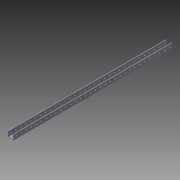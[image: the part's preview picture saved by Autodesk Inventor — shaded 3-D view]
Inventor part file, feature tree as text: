
AUTODESK INVENTOR PART (.ipt)
format: ipt  version: 2014 (Build 180170000, 170)  size: 183,296 bytes
history: native  units: in
note: dims shown in document units (in); Inventor stores cm internally (conversion verified against a paired STEP export)
features: sketch x3, hole x2, pattern_linear x2, extrude x1
ambient origin geometry x8: Origin, YZ Plane, XZ Plane, XY Plane, X Axis, Y Axis, Z Axis, Center Point
bodies: Solid1 (feature_tree)
feature tree (8):
  extrude  "Extrusion1"  Depth=1.125in
  hole  "Hole1"  [1 undecoded]
  pattern_linear  "Rectangular Pattern1"  Spacing1=0.5in  [1 undecoded]
  hole  "Hole2"  [1 undecoded]
  pattern_linear  "Rectangular Pattern2"  Spacing1=0.5in  [1 undecoded]
  sketch  "Sketch1"  dims[d0=1.25in d1=1.125in]
  sketch  "Sketch2"  dims[d4=0.0625in d5=0.125in]
  sketch  "Sketch3"  dims[d6=32.0in d7=0.0in d8=0.5in d9=0.25in d10=0.75in d11=0.375in d12=0.25in d13=0.5635in d14=1.0in d15=0.8108in d16=12.5984in d18=1.0in d19=0.5in d20=0.25in d21=0.75in d22=0.375in d23=0.25in d24=0.5635in d25=1.0in d26=0.8108in d27=12.5984in d29=1.0in]
note: 4 required parameter values undecoded (feature->parameter linkage not recoverable at this tier; creation-order binding heuristic only, values carry confidence <= 0.55)
